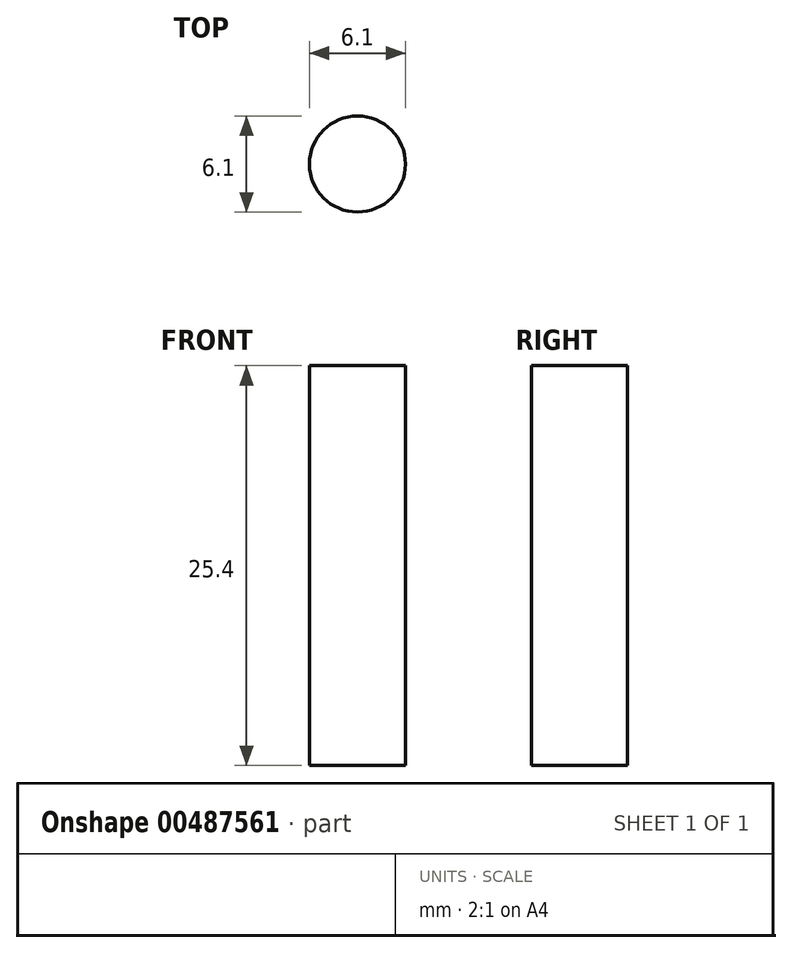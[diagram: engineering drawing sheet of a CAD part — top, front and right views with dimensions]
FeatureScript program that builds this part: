
annotation { "Feature Type Name" : "Feature", "Feature Type Description" : "" }
export const myFeature = defineFeature(function(context is Context, id is Id, definition is map)
    precondition{}
    {
        {
            var Q0;
            Q0=qCreatedBy(makeId("Top.planeOp"),FACE);
            var sketch = newSketch(context, id + "F0", { "sketchPlane" : qUnion([Q0])});
            skCircle(sketch, "E0", {"center": v(0, 0) * mm, "radius": 3.05 * mm});
            skSolve(sketch);
        }
        {
            var Q0;
            Q0 = qSketchRegion(id + "F0", true);
            extrude(context, id + "F1", {"entities" : qUnion([Q0]), "depth" : 25.4 * mm});
        }
    });
